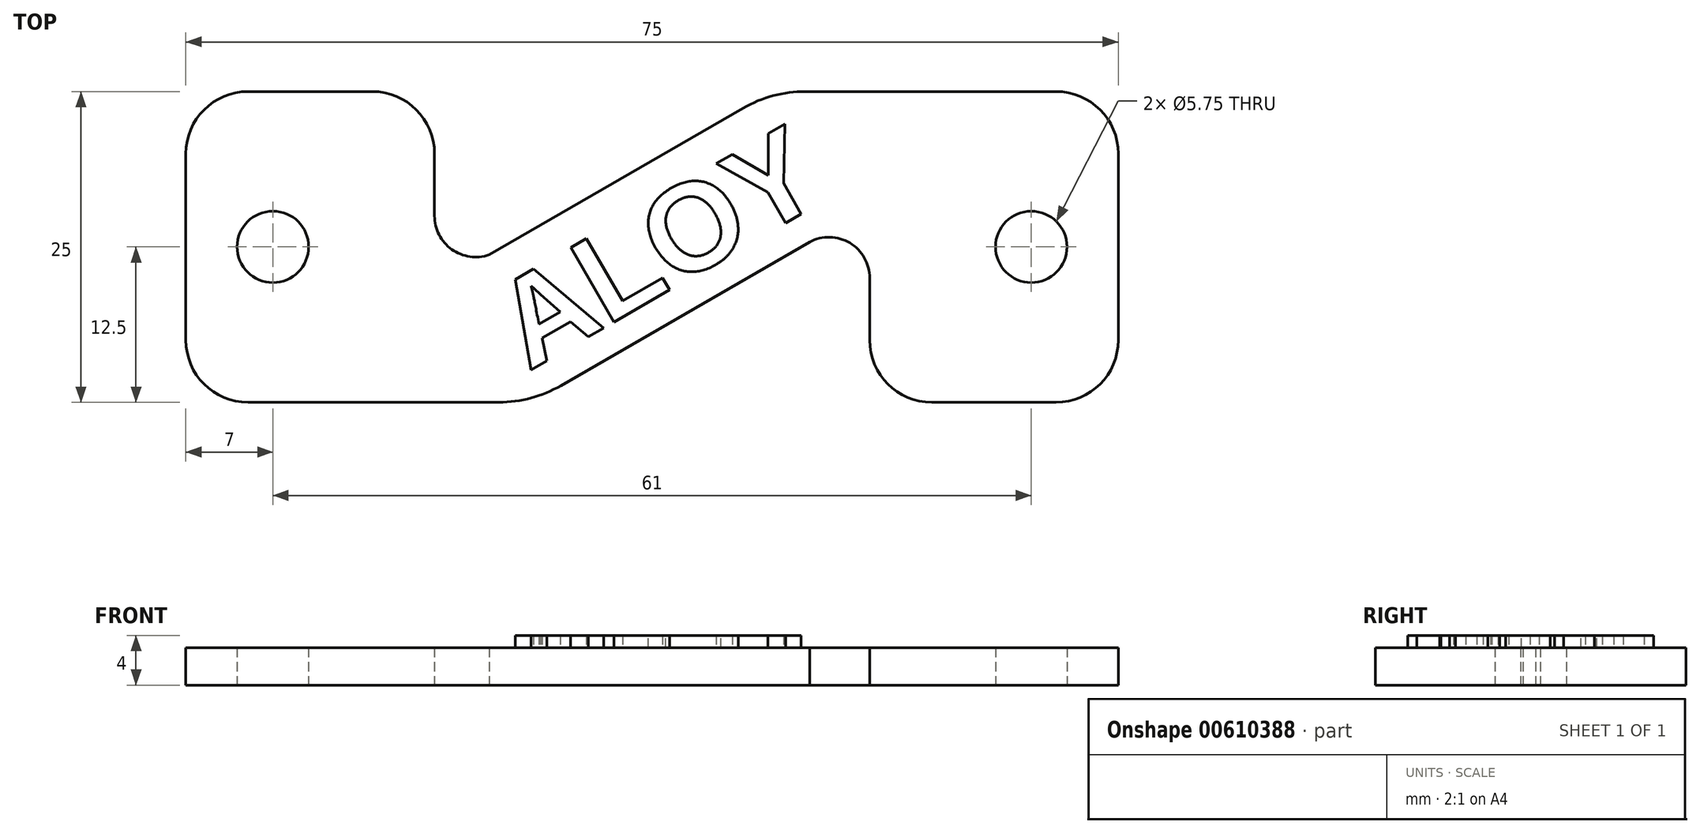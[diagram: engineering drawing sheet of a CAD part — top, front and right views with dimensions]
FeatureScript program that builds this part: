
annotation { "Feature Type Name" : "Feature", "Feature Type Description" : "" }
export const myFeature = defineFeature(function(context is Context, id is Id, definition is map)
    precondition{}
    {
        {
            var Q0;
            Q0=qCreatedBy(makeId("Top.planeOp"),FACE);
            var sketch = newSketch(context, id + "F0", { "sketchPlane" : qUnion([Q0])});
            skLineSegment(sketch, "E0.bottom", {"start": v(37.5, 12.5) * mm, "end": v(9.65, 12.5) * mm});
            skLineSegment(sketch, "E0.top", {"start": v(37.5, -12.5) * mm, "end": v(17.5, -12.5) * mm});
            skLineSegment(sketch, "E0.left", {"start": v(37.5, 12.5) * mm, "end": v(37.5, -12.5) * mm});
            skPoint(sketch, "E0.middle", {"position": v(0, 0) * mm});
            skLineSegment(sketch, "E1.0", {"start": v(-17.5, 12.5) * mm, "end": v(-17.5, 2.5) * mm});
            skLineSegment(sketch, "E2.0", {"start": v(17.5, -2.5) * mm, "end": v(17.5, -12.5) * mm});
            skLineSegment(sketch, "E3.trimOffspring", {"start": v(-9.65, -12.5) * mm, "end": v(-37.5, -12.5) * mm});
            skLineSegment(sketch, "E4.trimOffspring", {"start": v(-17.5, 12.5) * mm, "end": v(-37.5, 12.5) * mm});
            skLineSegment(sketch, "E5.trimOffspring", {"start": v(-37.5, 12.5) * mm, "end": v(-37.5, -12.5) * mm});
            skLineSegment(sketch, "E6.0", {"start": v(-30.5, 12.5) * mm, "end": v(-30.5, -12.5) * mm, "construction": true});
            skCircle(sketch, "E7", {"center": v(-30.5, 0) * mm, "radius": 2.88 * mm});
            skCircle(sketch, "E8.MirrorC", {"center": v(30.5, 0) * mm, "radius": 2.88 * mm});
            skLineSegment(sketch, "E9", {"start": v(-10.44, -6.03) * mm, "end": v(10.48, 6.05) * mm});
            skLineSegment(sketch, "E10.0", {"start": v(-9.65, -12.5) * mm, "end": v(13.48, 0.85) * mm});
            skLineSegment(sketch, "E11.0", {"start": v(-13.44, -0.83) * mm, "end": v(9.65, 12.5) * mm});
            skArc(sketch, "E12", {"start": v(-17.5, 2.5) * mm, "mid": v(-15.55, -0.52) * mm, "end": v(-12, 0) * mm});
            skArc(sketch, "E13", {"start": v(17.5, -2.5) * mm, "mid": v(15.9, 0.31) * mm, "end": v(12.68, 0.4) * mm});
            skSolve(sketch);
        }
        {
            var Q0;
            Q0=qSketchRegion(id+"F0",true);
            extrude(context, id + "F1", {"entities" : qUnion([Q0]), "depth" : 3 * mm, "offsetDistance" : 25 * mm});
        }
        {
            var Q0;
            Q0=makeQuery(id+"F1.opExtrude","SWEPT_EDGE",EDGE,{"disambiguationData":[OSD([sQuery(id+"F0.wireOp",EDGE,"E1.0"),sQuery(id+"F0.wireOp",EDGE,"E4.trimOffspring")])]});
            var Q1;
            Q1=makeQuery(id+"F1.opExtrude","SWEPT_EDGE",EDGE,{"disambiguationData":[OSD([sQuery(id+"F0.wireOp",EDGE,"E0.top"),sQuery(id+"F0.wireOp",EDGE,"E2.0")])]});
            var Q2;
            Q2=makeQuery(id+"F1.opExtrude","SWEPT_EDGE",EDGE,{"disambiguationData":[OSD([sQuery(id+"F0.wireOp",EDGE,"E0.top"),sQuery(id+"F0.wireOp",EDGE,"E0.left")])]});
            var Q3;
            Q3=makeQuery(id+"F1.opExtrude","SWEPT_EDGE",EDGE,{"disambiguationData":[OSD([sQuery(id+"F0.wireOp",EDGE,"E0.bottom"),sQuery(id+"F0.wireOp",EDGE,"E0.left")])]});
            var Q4;
            Q4=makeQuery(id+"F1.opExtrude","SWEPT_EDGE",EDGE,{"disambiguationData":[OSD([sQuery(id+"F0.wireOp",EDGE,"E3.trimOffspring"),sQuery(id+"F0.wireOp",EDGE,"E5.trimOffspring")])]});
            var Q5;
            Q5=makeQuery(id+"F1.opExtrude","SWEPT_EDGE",EDGE,{"disambiguationData":[OSD([sQuery(id+"F0.wireOp",EDGE,"E0.right"),sQuery(id+"F0.wireOp",EDGE,"E4.trimOffspring")])]});
            fillet(context, id + "F2", {"entities" : qUnion([Q0, Q1, Q2, Q3, Q4, Q5]), "radius" : 5 * mm, "tangentPropagation" : true, "allowEdgeOverflow" : false});
        }
        {
            var Q0;
            Q0=makeQuery(id+"F1.opExtrude","SWEPT_EDGE",EDGE,{"disambiguationData":[OSD([sQuery(id+"F0.wireOp",EDGE,"E3.trimOffspring"),sQuery(id+"F0.wireOp",EDGE,"E10.0")])]});
            var Q1;
            Q1=makeQuery(id+"F1.opExtrude","SWEPT_EDGE",EDGE,{"disambiguationData":[OSD([sQuery(id+"F0.wireOp",EDGE,"E0.bottom"),sQuery(id+"F0.wireOp",EDGE,"E11.0")])]});
            fillet(context, id + "F3", {"entities" : qUnion([Q0, Q1]), "radius" : 10 * mm, "tangentPropagation" : true, "allowEdgeOverflow" : false});
        }
        {
            var Q0;
            Q0=makeQuery(id+"F1.opExtrude","CAP_FACE",FACE,{"disambiguationData":[OSD([sQuery(id+"F0.wireOp",EDGE,"E0.bottom"),sQuery(id+"F0.wireOp",EDGE,"E0.top"),sQuery(id+"F0.wireOp",EDGE,"E0.left"),sQuery(id+"F0.wireOp",EDGE,"E1.0"),sQuery(id+"F0.wireOp",EDGE,"E2.0"),sQuery(id+"F0.wireOp",EDGE,"E3.trimOffspring"),sQuery(id+"F0.wireOp",EDGE,"E4.trimOffspring"),sQuery(id+"F0.wireOp",EDGE,"E5.trimOffspring"),sQuery(id+"F0.wireOp",EDGE,"E7"),sQuery(id+"F0.wireOp",EDGE,"E8.MirrorC"),sQuery(id+"F0.wireOp",EDGE,"E10.0"),sQuery(id+"F0.wireOp",EDGE,"E11.0"),sQuery(id+"F0.wireOp",EDGE,"E12"),sQuery(id+"F0.wireOp",EDGE,"E13")])],"isStart":false});
            var sketch = newSketch(context, id + "F4", { "sketchPlane" : qUnion([Q0])});
            skText(sketch, "E14", { "text": "ALOY", "fontName": "Arimo-Bold.ttf"});
            const initialGuessF4  = {"E14": [-0.00995, -0.01002, 0.86603, 0.5, 0.00725]};
            skSetInitialGuess(sketch, initialGuessF4);
            skSolve(sketch);
        }
        {
            var Q0;
            Q0 = qSketchRegion(id + "F4", true);
            extrude(context, id + "F5", {"entities" : qUnion([Q0]), "operationType" : NewBodyOperationType.ADD, "depth" : 1 * mm, "offsetDistance" : 25 * mm});
        }
    });
